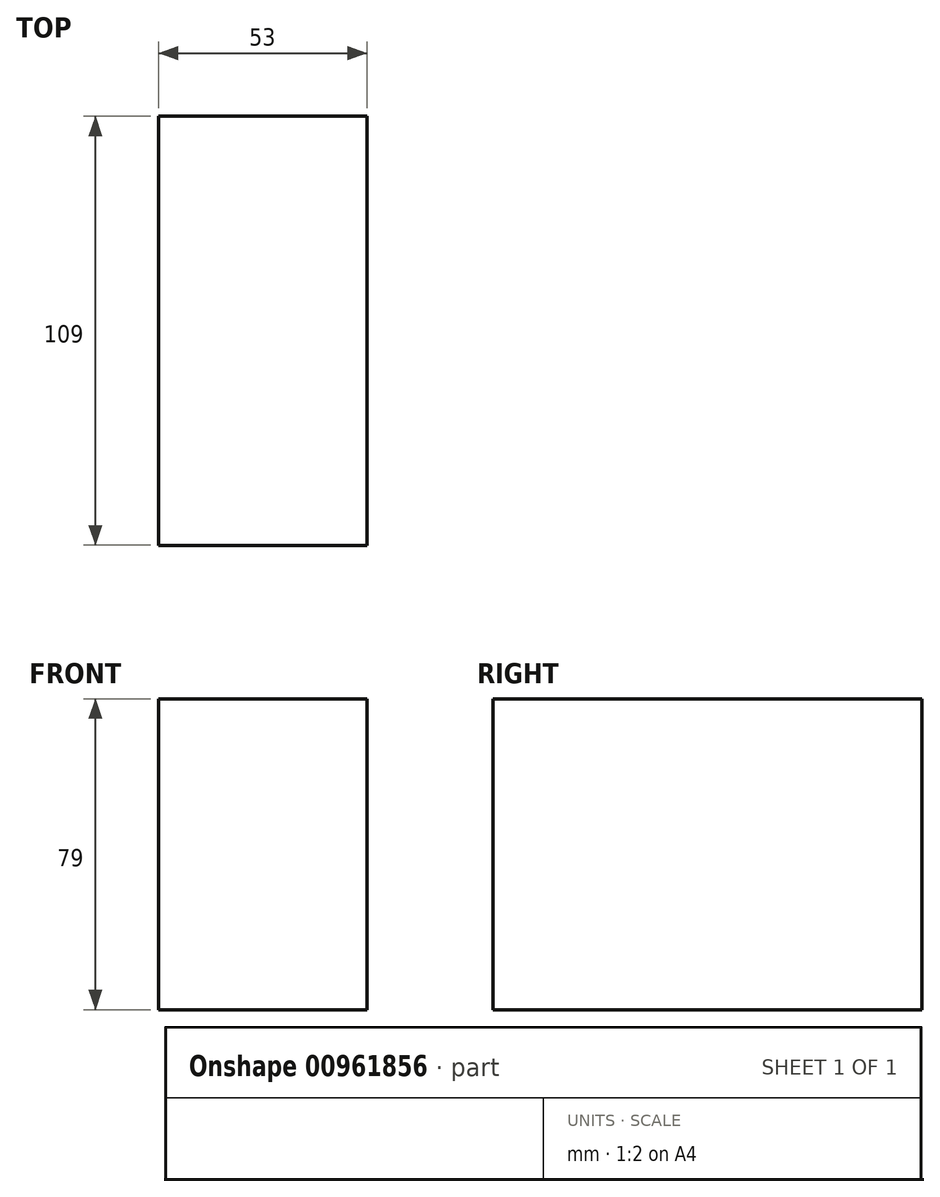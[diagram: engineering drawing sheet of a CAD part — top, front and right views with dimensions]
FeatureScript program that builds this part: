
annotation { "Feature Type Name" : "Feature", "Feature Type Description" : "" }
export const myFeature = defineFeature(function(context is Context, id is Id, definition is map)
    precondition{}
    {
        {
            var Q0;
            Q0=qCreatedBy(makeId("Top.planeOp"),FACE);
            var sketch = newSketch(context, id + "F0", { "sketchPlane" : qUnion([Q0])});
            skLineSegment(sketch, "E0.bottom", {"start": v(-49.36, 71.53) * mm, "end": v(3.64, 71.53) * mm});
            skLineSegment(sketch, "E0.top", {"start": v(-49.36, -37.47) * mm, "end": v(3.64, -37.47) * mm});
            skLineSegment(sketch, "E0.left", {"start": v(-49.36, 71.53) * mm, "end": v(-49.36, -37.47) * mm});
            skLineSegment(sketch, "E0.right", {"start": v(3.64, 71.53) * mm, "end": v(3.64, -37.47) * mm});
            skSolve(sketch);
        }
        {
            var Q0;
            Q0 = qSketchRegion(id + "F0", true);
            extrude(context, id + "F1", {"entities" : qUnion([Q0]), "depth" : 79 * mm, "offsetDistance" : 25 * mm});
        }
    });
